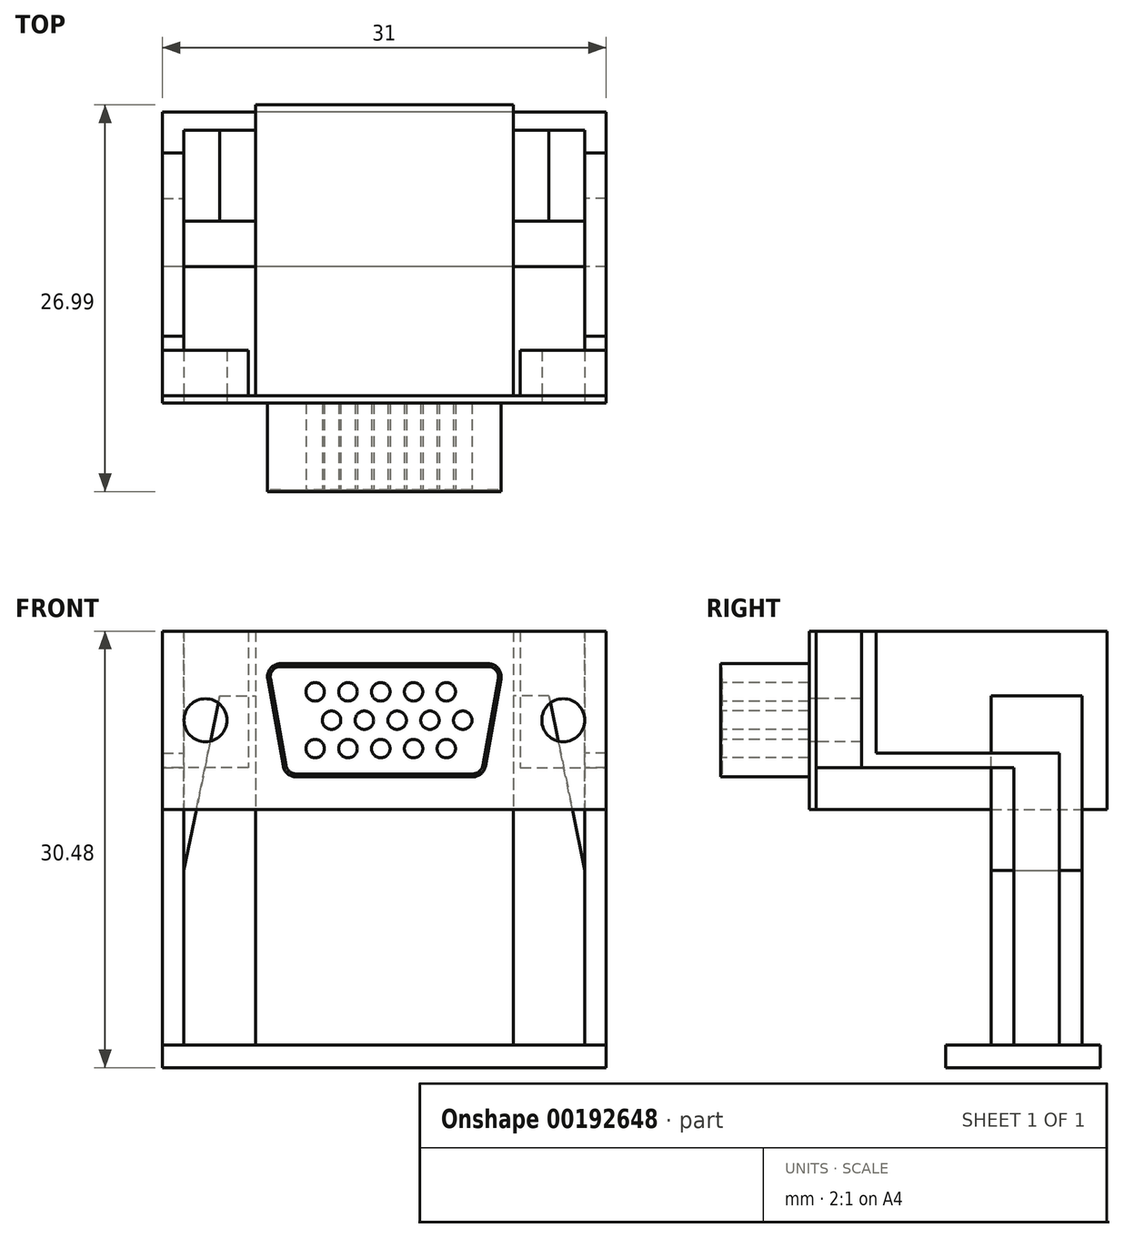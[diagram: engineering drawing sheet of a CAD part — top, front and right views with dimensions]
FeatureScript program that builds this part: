
annotation { "Feature Type Name" : "Feature", "Feature Type Description" : "" }
export const myFeature = defineFeature(function(context is Context, id is Id, definition is map)
    precondition{}
    {
        {
            var Q0;
            Q0=qCreatedBy(makeId("Right.planeOp"),FACE);
            var sketch = newSketch(context, id + "F0", { "sketchPlane" : qUnion([Q0])});
            skLineSegment(sketch, "E0.bottom", {"start": v(0, 30.48) * mm, "end": v(0.5, 30.48) * mm});
            skLineSegment(sketch, "E0.top", {"start": v(0, 18.03) * mm, "end": v(0.5, 18.03) * mm});
            skLineSegment(sketch, "E0.left", {"start": v(0, 30.48) * mm, "end": v(0, 18.03) * mm});
            skLineSegment(sketch, "E0.right", {"start": v(0.5, 30.48) * mm, "end": v(0.5, 18.03) * mm});
            skLineSegment(sketch, "E1.bottom", {"start": v(9.53, 0) * mm, "end": v(20.32, 0) * mm});
            skLineSegment(sketch, "E1.top", {"start": v(9.53, 1.59) * mm, "end": v(20.32, 1.59) * mm});
            skLineSegment(sketch, "E1.left", {"start": v(9.53, 0) * mm, "end": v(9.53, 1.59) * mm});
            skLineSegment(sketch, "E1.right", {"start": v(20.32, 0) * mm, "end": v(20.32, 1.59) * mm});
            skSolve(sketch);
        }
        {
            var Q0;
            Q0 = qSketchRegion(id + "F0", true);
            extrude(context, id + "F1", {"entities" : qUnion([Q0]), "endBound" : BoundingType.SYMMETRIC, "depth" : 31 * mm});
        }
        {
            var Q0;
            Q0=makeQuery(id+"F1.opExtrude","CAP_FACE",FACE,{"disambiguationData":[OSD([sQuery(id+"F0.wireOp",EDGE,"E0.bottom"),sQuery(id+"F0.wireOp",EDGE,"E0.top"),sQuery(id+"F0.wireOp",EDGE,"E0.left"),sQuery(id+"F0.wireOp",EDGE,"E0.right")])],"isStart":false});
            var sketch = newSketch(context, id + "F2", { "sketchPlane" : qUnion([Q0])});
            skLineSegment(sketch, "E2.bottom", {"start": v(0.5, 30.48) * mm, "end": v(3.68, 30.48) * mm});
            skLineSegment(sketch, "E2.top", {"start": v(0.5, 20.96) * mm, "end": v(3.68, 20.96) * mm});
            skLineSegment(sketch, "E2.left", {"start": v(0.5, 30.48) * mm, "end": v(0.5, 20.96) * mm});
            skLineSegment(sketch, "E2.right", {"start": v(3.68, 30.48) * mm, "end": v(3.68, 20.96) * mm});
            skSolve(sketch);
        }
        {
            var Q0;
            Q0 = qSketchRegion(id + "F2", true);
            extrude(context, id + "F3", {"entities" : qUnion([Q0]), "oppositeDirection" : true, "depth" : 6 * mm});
        }
        {
            var Q0;
            Q0=qCreatedBy(makeId("Right.planeOp"),FACE);
            var sketch = newSketch(context, id + "F4", { "sketchPlane" : qUnion([Q0])});
            skLineSegment(sketch, "E3.bottom", {"start": v(0.5, 30.48) * mm, "end": v(20.82, 30.48) * mm});
            skLineSegment(sketch, "E3.top", {"start": v(0.5, 18.03) * mm, "end": v(20.82, 18.03) * mm});
            skLineSegment(sketch, "E3.left", {"start": v(0.5, 30.48) * mm, "end": v(0.5, 18.03) * mm});
            skLineSegment(sketch, "E3.right", {"start": v(20.82, 30.48) * mm, "end": v(20.82, 18.03) * mm});
            skSolve(sketch);
        }
        {
            var Q0;
            Q0 = qSketchRegion(id + "F4", true);
            extrude(context, id + "F5", {"entities" : qUnion([Q0]), "endBound" : BoundingType.SYMMETRIC, "depth" : 18 * mm});
        }
        {
            var Q0;
            Q0=makeQuery(id+"F5.opExtrude","CAP_FACE",FACE,{"disambiguationData":[OSD([sQuery(id+"F4.wireOp",EDGE,"E3.bottom"),sQuery(id+"F4.wireOp",EDGE,"E3.top"),sQuery(id+"F4.wireOp",EDGE,"E3.left"),sQuery(id+"F4.wireOp",EDGE,"E3.right")])],"isStart":false});
            var sketch = newSketch(context, id + "F6", { "sketchPlane" : qUnion([Q0])});
            skLineSegment(sketch, "E4.bottom", {"start": v(12.7, 25.97) * mm, "end": v(19.05, 25.97) * mm});
            skLineSegment(sketch, "E4.top", {"start": v(12.7, 1.59) * mm, "end": v(19.05, 1.59) * mm});
            skLineSegment(sketch, "E4.left", {"start": v(12.7, 25.97) * mm, "end": v(12.7, 1.59) * mm});
            skLineSegment(sketch, "E4.right", {"start": v(19.05, 25.97) * mm, "end": v(19.05, 1.59) * mm});
            skSolve(sketch);
        }
        {
            var Q0;
            Q0 = qSketchRegion(id + "F6", true);
            extrude(context, id + "F7", {"entities" : qUnion([Q0]), "depth" : 5 * mm});
        }
        {
            var Q0;
            Q0=makeQuery(id+"F7.opExtrude","SWEPT_FACE",FACE,{"disambiguationData":[OSD([sQuery(id+"F6.wireOp",EDGE,"E4.right")])]});
            var sketch = newSketch(context, id + "F8", { "sketchPlane" : qUnion([Q0])});
            skLineSegment(sketch, "E5", {"start": v(-11.5, 25.97) * mm, "end": v(-14, 13.78) * mm});
            skLineSegment(sketch, "E6", {"start": v(-14, 13.78) * mm, "end": v(-14, 25.97) * mm});
            skLineSegment(sketch, "E7", {"start": v(-14, 25.97) * mm, "end": v(-11.5, 25.97) * mm});
            skSolve(sketch);
        }
        {
            var Q0;
            Q0 = qSketchRegion(id + "F8", true);
            extrude(context, id + "F9", {"entities" : qUnion([Q0]), "operationType" : NewBodyOperationType.REMOVE, "endBound" : BoundingType.UP_TO_NEXT, "oppositeDirection" : true, "depth" : 25.4 * mm});
        }
        {
            var Q0;
            Q0=makeQuery(id+"F7.opExtrude","CAP_FACE",FACE,{"disambiguationData":[OSD([sQuery(id+"F6.wireOp",EDGE,"E4.bottom"),sQuery(id+"F6.wireOp",EDGE,"E4.top"),sQuery(id+"F6.wireOp",EDGE,"E4.left"),sQuery(id+"F6.wireOp",EDGE,"E4.right")])],"isStart":false});
            var sketch = newSketch(context, id + "F10", { "sketchPlane" : qUnion([Q0])});
            skLineSegment(sketch, "E8", {"start": v(17.46, 1.59) * mm, "end": v(17.46, 21.96) * mm});
            skLineSegment(sketch, "E9", {"start": v(17.46, 21.96) * mm, "end": v(4.68, 21.96) * mm});
            skLineSegment(sketch, "E10", {"start": v(4.68, 21.96) * mm, "end": v(4.68, 30.48) * mm});
            skLineSegment(sketch, "E11", {"start": v(4.68, 30.48) * mm, "end": v(3.68, 30.48) * mm});
            skLineSegment(sketch, "E12", {"start": v(3.68, 30.48) * mm, "end": v(3.68, 20.96) * mm});
            skLineSegment(sketch, "E13", {"start": v(3.68, 20.96) * mm, "end": v(14.29, 20.96) * mm});
            skLineSegment(sketch, "E14", {"start": v(14.29, 20.96) * mm, "end": v(14.29, 1.59) * mm});
            skLineSegment(sketch, "E15", {"start": v(14.29, 1.59) * mm, "end": v(17.46, 1.59) * mm});
            skLineSegment(sketch, "E16", {"start": v(15.87, 1.59) * mm, "end": v(15.87, 25.97) * mm, "construction": true});
            skLineSegment(sketch, "E17", {"start": v(14.29, 20.96) * mm, "end": v(14.29, 21.96) * mm, "construction": true});
            skSolve(sketch);
        }
        {
            var Q0;
            Q0 = qSketchRegion(id + "F10", true);
            var Q1;
            Q1=makeQuery(id+"F3.opExtrude","CAP_FACE",FACE,{"disambiguationData":[OSD([sQuery(id+"F2.wireOp",EDGE,"E2.bottom"),sQuery(id+"F2.wireOp",EDGE,"E2.top"),sQuery(id+"F2.wireOp",EDGE,"E2.left"),sQuery(id+"F2.wireOp",EDGE,"E2.right")])],"isStart":true});
            extrude(context, id + "F11", {"entities" : qUnion([Q0]), "endBound" : BoundingType.UP_TO_SURFACE, "endBoundEntityFace" : qUnion([Q1]), "depth" : 25.4 * mm});
        }
        {
            var Q0;
            Q0=makeQuery(id+"F3.opExtrude","SWEPT_BODY",BODY,{"disambiguationData":[OSD([sQuery(id+"F2.wireOp",EDGE,"E2.bottom"),sQuery(id+"F2.wireOp",EDGE,"E2.top"),sQuery(id+"F2.wireOp",EDGE,"E2.left"),sQuery(id+"F2.wireOp",EDGE,"E2.right")])]});
            var Q1;
            Q1=makeQuery(id+"F11.opExtrude","SWEPT_BODY",BODY,{"disambiguationData":[OSD([sQuery(id+"F10.wireOp",EDGE,"E8"),sQuery(id+"F10.wireOp",EDGE,"E9"),sQuery(id+"F10.wireOp",EDGE,"E10"),sQuery(id+"F10.wireOp",EDGE,"E11"),sQuery(id+"F10.wireOp",EDGE,"E12"),sQuery(id+"F10.wireOp",EDGE,"E13"),sQuery(id+"F10.wireOp",EDGE,"E14"),sQuery(id+"F10.wireOp",EDGE,"E15")])]});
            var Q2;
            Q2=makeQuery(id+"F7.opExtrude","SWEPT_BODY",BODY,{"disambiguationData":[OSD([sQuery(id+"F6.wireOp",EDGE,"E4.bottom"),sQuery(id+"F6.wireOp",EDGE,"E4.top"),sQuery(id+"F6.wireOp",EDGE,"E4.left"),sQuery(id+"F6.wireOp",EDGE,"E4.right")])]});
            var Q3;
            Q3=qCreatedBy(makeId("Right.planeOp"),FACE);
            mirror(context, id + "F12", {"entities" : qUnion([Q0, Q1, Q2]), "mirrorPlane" : qUnion([Q3])});
        }
        {
            var Q0;
            Q0=makeQuery(id+"F1.opExtrude","SWEPT_FACE",FACE,{"disambiguationData":[OSD([sQuery(id+"F0.wireOp",EDGE,"E0.left")])]});
            var sketch = newSketch(context, id + "F18", { "sketchPlane" : qUnion([Q0])});
            skLineSegment(sketch, "E18", {"start": v(-7.25, 28.2) * mm, "end": v(7.25, 28.2) * mm});
            skLineSegment(sketch, "E19", {"start": v(-6.17, 20.3) * mm, "end": v(6.17, 20.3) * mm});
            skLineSegment(sketch, "E20", {"start": v(-8.15, 27.13) * mm, "end": v(-7.07, 21.06) * mm});
            skLineSegment(sketch, "E21", {"start": v(8.15, 27.13) * mm, "end": v(7.07, 21.06) * mm});
            skArc(sketch, "E22", {"start": v(-7.25, 28.2) * mm, "mid": v(-7.95, 27.88) * mm, "end": v(-8.15, 27.13) * mm});
            skArc(sketch, "E23", {"start": v(8.15, 27.13) * mm, "mid": v(7.95, 27.88) * mm, "end": v(7.25, 28.2) * mm});
            skArc(sketch, "E24", {"start": v(6.17, 20.3) * mm, "mid": v(6.75, 20.52) * mm, "end": v(7.07, 21.06) * mm});
            skArc(sketch, "E25", {"start": v(-7.07, 21.06) * mm, "mid": v(-6.75, 20.52) * mm, "end": v(-6.17, 20.3) * mm});
            skLineSegment(sketch, "E26", {"start": v(-15.5, 24.26) * mm, "end": v(15.5, 24.26) * mm, "construction": true});
            skCircle(sketch, "E27", {"center": v(12.23, 24.26) * mm, "radius": 1.5 * mm, "construction": true});
            skCircle(sketch, "E28", {"center": v(-4.38, 24.26) * mm, "radius": 0.64 * mm, "construction": true});
            skSolve(sketch);
        }
        {
            var Q0;
            Q0 = qSketchRegion(id + "F18", true);
            extrude(context, id + "F19", {"entities" : qUnion([Q0]), "depth" : 6.17 * mm});
        }
        {
            var Q0;
            Q0=makeQuery(id+"F19.opExtrude","CAP_FACE",FACE,{"disambiguationData":[OSD([sQuery(id+"F18.wireOp",EDGE,"E18"),sQuery(id+"F18.wireOp",EDGE,"E19"),sQuery(id+"F18.wireOp",EDGE,"E20"),sQuery(id+"F18.wireOp",EDGE,"E21"),sQuery(id+"F18.wireOp",EDGE,"E22"),sQuery(id+"F18.wireOp",EDGE,"E23"),sQuery(id+"F18.wireOp",EDGE,"E24"),sQuery(id+"F18.wireOp",EDGE,"E25")])],"isStart":false});
            var sketch = newSketch(context, id + "F13", { "sketchPlane" : qUnion([Q0])});
            skArc(sketch, "E29.0", {"start": v(-6.87, 21.1) * mm, "mid": v(-6.63, 20.67) * mm, "end": v(-6.17, 20.5) * mm});
            skLineSegment(sketch, "E29.1", {"start": v(-7.95, 27.17) * mm, "end": v(-6.87, 21.1) * mm});
            skLineSegment(sketch, "E29.2", {"start": v(-6.17, 20.5) * mm, "end": v(6.17, 20.5) * mm});
            skArc(sketch, "E29.3", {"start": v(-7.25, 28) * mm, "mid": v(-7.8, 27.75) * mm, "end": v(-7.95, 27.17) * mm});
            skArc(sketch, "E29.4", {"start": v(6.17, 20.5) * mm, "mid": v(6.63, 20.67) * mm, "end": v(6.87, 21.1) * mm});
            skLineSegment(sketch, "E29.5", {"start": v(7.95, 27.17) * mm, "end": v(6.87, 21.1) * mm});
            skArc(sketch, "E29.6", {"start": v(7.95, 27.17) * mm, "mid": v(7.8, 27.75) * mm, "end": v(7.25, 28) * mm});
            skLineSegment(sketch, "E29.7", {"start": v(-7.25, 28) * mm, "end": v(7.25, 28) * mm});
            skSolve(sketch);
        }
        {
            var Q0;
            Q0 = qSketchRegion(id + "F13", true);
            extrude(context, id + "F14", {"entities" : qUnion([Q0]), "operationType" : NewBodyOperationType.REMOVE, "oppositeDirection" : true, "depth" : 0.1 * mm});
        }
        {
            var Q0;
            Q0=makeQuery(id+"F14.boolean.opBoolean","COPY",FACE,{"derivedFrom":makeQuery(id+"F14.opExtrude","CAP_FACE",FACE,{"disambiguationData":[OSD([sQuery(id+"F13.wireOp",EDGE,"E29.0"),sQuery(id+"F13.wireOp",EDGE,"E29.1"),sQuery(id+"F13.wireOp",EDGE,"E29.2"),sQuery(id+"F13.wireOp",EDGE,"E29.3"),sQuery(id+"F13.wireOp",EDGE,"E29.4"),sQuery(id+"F13.wireOp",EDGE,"E29.5"),sQuery(id+"F13.wireOp",EDGE,"E29.6"),sQuery(id+"F13.wireOp",EDGE,"E29.7")])],"isStart":false})});
            var sketch = newSketch(context, id + "F15", { "sketchPlane" : qUnion([Q0])});
            skLineSegment(sketch, "E30", {"start": v(-4.83, 26.24) * mm, "end": v(4.33, 26.24) * mm, "construction": true});
            skLineSegment(sketch, "E31", {"start": v(-3.69, 24.26) * mm, "end": v(5.48, 24.26) * mm, "construction": true});
            skLineSegment(sketch, "E32", {"start": v(-4.83, 22.28) * mm, "end": v(4.33, 22.28) * mm, "construction": true});
            skCircle(sketch, "E33", {"center": v(-2.54, 26.24) * mm, "radius": 0.65 * mm});
            skCircle(sketch, "E34", {"center": v(-3.69, 24.26) * mm, "radius": 0.65 * mm});
            skCircle(sketch, "E35", {"center": v(-4.83, 26.24) * mm, "radius": 0.65 * mm});
            skLineSegment(sketch, "E36", {"start": v(-0.25, 26.24) * mm, "end": v(-0.25, 22.28) * mm, "construction": true});
            skPoint(sketch, "E37", {"position": v(0, 22.28) * mm});
            skCircle(sketch, "E38", {"center": v(-0.25, 26.24) * mm, "radius": 0.65 * mm});
            skCircle(sketch, "E39", {"center": v(2.04, 26.24) * mm, "radius": 0.65 * mm});
            skCircle(sketch, "E40", {"center": v(5.48, 24.26) * mm, "radius": 0.65 * mm});
            skCircle(sketch, "E41", {"center": v(-1.4, 24.26) * mm, "radius": 0.65 * mm});
            skCircle(sketch, "E42", {"center": v(3.19, 24.26) * mm, "radius": 0.65 * mm});
            skCircle(sketch, "E43", {"center": v(0.9, 24.26) * mm, "radius": 0.65 * mm});
            skCircle(sketch, "E44.MirrorC", {"center": v(2.04, 22.28) * mm, "radius": 0.65 * mm});
            skCircle(sketch, "E45.MirrorC", {"center": v(-0.25, 22.28) * mm, "radius": 0.65 * mm});
            skCircle(sketch, "E46.MirrorC", {"center": v(-4.83, 22.28) * mm, "radius": 0.65 * mm});
            skLineSegment(sketch, "E47", {"start": v(-2.54, 22.28) * mm, "end": v(-2.54, 26.24) * mm, "construction": true});
            skLineSegment(sketch, "E48", {"start": v(2.04, 26.24) * mm, "end": v(2.04, 22.28) * mm, "construction": true});
            skLineSegment(sketch, "E49.MirrorCS", {"start": v(4.33, 26.24) * mm, "end": v(4.33, 22.28) * mm, "construction": true});
            skCircle(sketch, "E50", {"center": v(4.33, 22.28) * mm, "radius": 0.65 * mm});
            skCircle(sketch, "E51", {"center": v(4.33, 26.24) * mm, "radius": 0.65 * mm});
            skCircle(sketch, "E52", {"center": v(-2.54, 22.28) * mm, "radius": 0.65 * mm});
            skSolve(sketch);
        }
        {
            var Q0;
            Q0 = qSketchRegion(id + "F15", true);
            extrude(context, id + "F16", {"entities" : qUnion([Q0]), "operationType" : NewBodyOperationType.REMOVE, "endBound" : BoundingType.UP_TO_NEXT, "oppositeDirection" : true, "depth" : 25.4 * mm});
        }
        {
            var Q0;
            Q0=makeQuery(id+"F18.imprint","IMPRINT",FACE,{"disambiguationData":[TD([[makeQuery(id+"F18.imprint","IMPRINT",EDGE,{"derivedFrom":sQuery(id+"F18.wireOp",EDGE,"E18")}),1.0]])]});
            var sketch = newSketch(context, id + "F17", { "sketchPlane" : qUnion([Q0])});
            skCircle(sketch, "E53", {"center": v(-12.5, 24.26) * mm, "radius": 1.5 * mm});
            skCircle(sketch, "E54", {"center": v(12.5, 24.26) * mm, "radius": 1.5 * mm});
            skSolve(sketch);
        }
        {
            var Q0;
            Q0 = qSketchRegion(id + "F17", true);
            var Q1;
            Q1=makeQuery(id+"F3.opExtrude","SWEPT_FACE",FACE,{"disambiguationData":[OSD([sQuery(id+"F2.wireOp",EDGE,"E2.right")])]});
            extrude(context, id + "F20", {"entities" : qUnion([Q0]), "operationType" : NewBodyOperationType.REMOVE, "endBound" : BoundingType.UP_TO_SURFACE, "oppositeDirection" : true, "endBoundEntityFace" : qUnion([Q1]), "depth" : 25.4 * mm});
        }
    });
